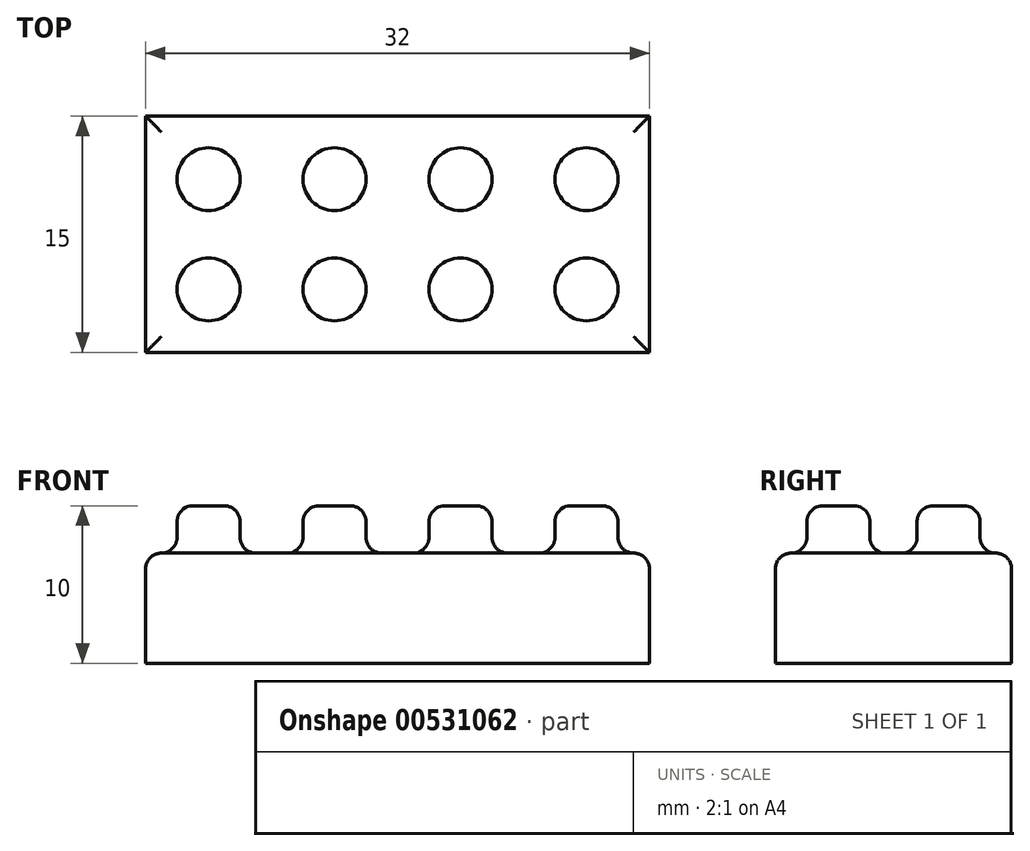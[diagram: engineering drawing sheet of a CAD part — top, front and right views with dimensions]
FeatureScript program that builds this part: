
annotation { "Feature Type Name" : "Feature", "Feature Type Description" : "" }
export const myFeature = defineFeature(function(context is Context, id is Id, definition is map)
    precondition{}
    {
        {
            var Q0;
            Q0=qCreatedBy(makeId("Top.planeOp"),FACE);
            var sketch = newSketch(context, id + "F0", { "sketchPlane" : qUnion([Q0])});
            skLineSegment(sketch, "E0.bottom", {"start": v(-16, 7.5) * mm, "end": v(16, 7.5) * mm});
            skLineSegment(sketch, "E0.top", {"start": v(-16, -7.5) * mm, "end": v(16, -7.5) * mm});
            skLineSegment(sketch, "E0.left", {"start": v(-16, 7.5) * mm, "end": v(-16, -7.5) * mm});
            skLineSegment(sketch, "E0.right", {"start": v(16, 7.5) * mm, "end": v(16, -7.5) * mm});
            skSolve(sketch);
        }
        {
            var Q0;
            Q0 = qSketchRegion(id + "F0", true);
            extrude(context, id + "F1", {"entities" : qUnion([Q0]), "depth" : 7 * mm, "offsetDistance" : 25 * mm});
        }
        {
            var Q0;
            Q0=makeQuery(id+"F1.opExtrude","CAP_FACE",FACE,{"disambiguationData":[OSD([sQuery(id+"F0.wireOp",EDGE,"E0.bottom"),sQuery(id+"F0.wireOp",EDGE,"E0.top"),sQuery(id+"F0.wireOp",EDGE,"E0.left"),sQuery(id+"F0.wireOp",EDGE,"E0.right")])],"isStart":false});
            var sketch = newSketch(context, id + "F2", { "sketchPlane" : qUnion([Q0])});
            skCircle(sketch, "E1", {"center": v(-12, -3.5) * mm, "radius": 2 * mm});
            skCircle(sketch, "E2", {"center": v(-4, -3.5) * mm, "radius": 2 * mm});
            skCircle(sketch, "E3", {"center": v(4, -3.5) * mm, "radius": 2 * mm});
            skCircle(sketch, "E4", {"center": v(12, -3.5) * mm, "radius": 2 * mm});
            skCircle(sketch, "E5", {"center": v(-12, 3.5) * mm, "radius": 2 * mm});
            skCircle(sketch, "E6", {"center": v(-4, 3.5) * mm, "radius": 2 * mm});
            skCircle(sketch, "E7", {"center": v(4, 3.5) * mm, "radius": 2 * mm});
            skCircle(sketch, "E8", {"center": v(12, 3.5) * mm, "radius": 2 * mm});
            skSolve(sketch);
        }
        {
            var Q0;
            Q0=makeQuery(id+"F2.imprint","IMPRINT",FACE,{"disambiguationData":[TD([[makeQuery(id+"F2.imprint","IMPRINT",EDGE,{"derivedFrom":sQuery(id+"F2.wireOp",EDGE,"E5")}),1.0]])]});
            var Q1;
            Q1=makeQuery(id+"F2.imprint","IMPRINT",FACE,{"disambiguationData":[TD([[makeQuery(id+"F2.imprint","IMPRINT",EDGE,{"derivedFrom":sQuery(id+"F2.wireOp",EDGE,"E1")}),1.0]])]});
            var Q2;
            Q2=makeQuery(id+"F2.imprint","IMPRINT",FACE,{"disambiguationData":[TD([[makeQuery(id+"F2.imprint","IMPRINT",EDGE,{"derivedFrom":sQuery(id+"F2.wireOp",EDGE,"E6")}),1.0]])]});
            var Q3;
            Q3=makeQuery(id+"F2.imprint","IMPRINT",FACE,{"disambiguationData":[TD([[makeQuery(id+"F2.imprint","IMPRINT",EDGE,{"derivedFrom":sQuery(id+"F2.wireOp",EDGE,"E2")}),1.0]])]});
            var Q4;
            Q4=makeQuery(id+"F2.imprint","IMPRINT",FACE,{"disambiguationData":[TD([[makeQuery(id+"F2.imprint","IMPRINT",EDGE,{"derivedFrom":sQuery(id+"F2.wireOp",EDGE,"E3")}),1.0]])]});
            var Q5;
            Q5=makeQuery(id+"F2.imprint","IMPRINT",FACE,{"disambiguationData":[TD([[makeQuery(id+"F2.imprint","IMPRINT",EDGE,{"derivedFrom":sQuery(id+"F2.wireOp",EDGE,"E7")}),1.0]])]});
            var Q6;
            Q6=makeQuery(id+"F2.imprint","IMPRINT",FACE,{"disambiguationData":[TD([[makeQuery(id+"F2.imprint","IMPRINT",EDGE,{"derivedFrom":sQuery(id+"F2.wireOp",EDGE,"E8")}),1.0]])]});
            var Q7;
            Q7=makeQuery(id+"F2.imprint","IMPRINT",FACE,{"disambiguationData":[TD([[makeQuery(id+"F2.imprint","IMPRINT",EDGE,{"derivedFrom":sQuery(id+"F2.wireOp",EDGE,"E4")}),1.0]])]});
            extrude(context, id + "F3", {"entities" : qUnion([Q0, Q1, Q2, Q3, Q4, Q5, Q6, Q7]), "operationType" : NewBodyOperationType.ADD, "depth" : 3 * mm, "offsetDistance" : 25 * mm});
        }
        {
            var Q0;
            Q0=makeQuery(id+"F1.opExtrude","CAP_FACE",FACE,{"disambiguationData":[OSD([sQuery(id+"F0.wireOp",EDGE,"E0.bottom"),sQuery(id+"F0.wireOp",EDGE,"E0.top"),sQuery(id+"F0.wireOp",EDGE,"E0.left"),sQuery(id+"F0.wireOp",EDGE,"E0.right")])],"isStart":false});
            var Q1;
            Q1=makeQuery(id+"F3.opExtrude","CAP_FACE",FACE,{"disambiguationData":[OSD([sQuery(id+"F2.wireOp",EDGE,"E1")])],"isStart":false});
            var Q2;
            Q2=makeQuery(id+"F3.opExtrude","CAP_FACE",FACE,{"disambiguationData":[OSD([sQuery(id+"F2.wireOp",EDGE,"E5")])],"isStart":false});
            var Q3;
            Q3=makeQuery(id+"F3.opExtrude","CAP_FACE",FACE,{"disambiguationData":[OSD([sQuery(id+"F2.wireOp",EDGE,"E6")])],"isStart":false});
            var Q4;
            Q4=makeQuery(id+"F3.opExtrude","CAP_FACE",FACE,{"disambiguationData":[OSD([sQuery(id+"F2.wireOp",EDGE,"E2")])],"isStart":false});
            var Q5;
            Q5=makeQuery(id+"F3.opExtrude","CAP_FACE",FACE,{"disambiguationData":[OSD([sQuery(id+"F2.wireOp",EDGE,"E3")])],"isStart":false});
            var Q6;
            Q6=makeQuery(id+"F3.opExtrude","CAP_EDGE",EDGE,{"disambiguationData":[OSD([sQuery(id+"F2.wireOp",EDGE,"E7")])],"isStart":false});
            var Q7;
            Q7=makeQuery(id+"F3.opExtrude","CAP_FACE",FACE,{"disambiguationData":[OSD([sQuery(id+"F2.wireOp",EDGE,"E8")])],"isStart":false});
            var Q8;
            Q8=makeQuery(id+"F3.opExtrude","CAP_FACE",FACE,{"disambiguationData":[OSD([sQuery(id+"F2.wireOp",EDGE,"E4")])],"isStart":false});
            var Q9;
            Q9=makeQuery(id+"F3.opExtrude","CAP_FACE",FACE,{"disambiguationData":[OSD([sQuery(id+"F2.wireOp",EDGE,"E7")])],"isStart":false});
            fillet(context, id + "F4", {"entities" : qUnion([Q0, Q1, Q2, Q3, Q4, Q5, Q6, Q7, Q8, Q9]), "radius" : 1 * mm, "tangentPropagation" : true, "allowEdgeOverflow" : false});
        }
    });
